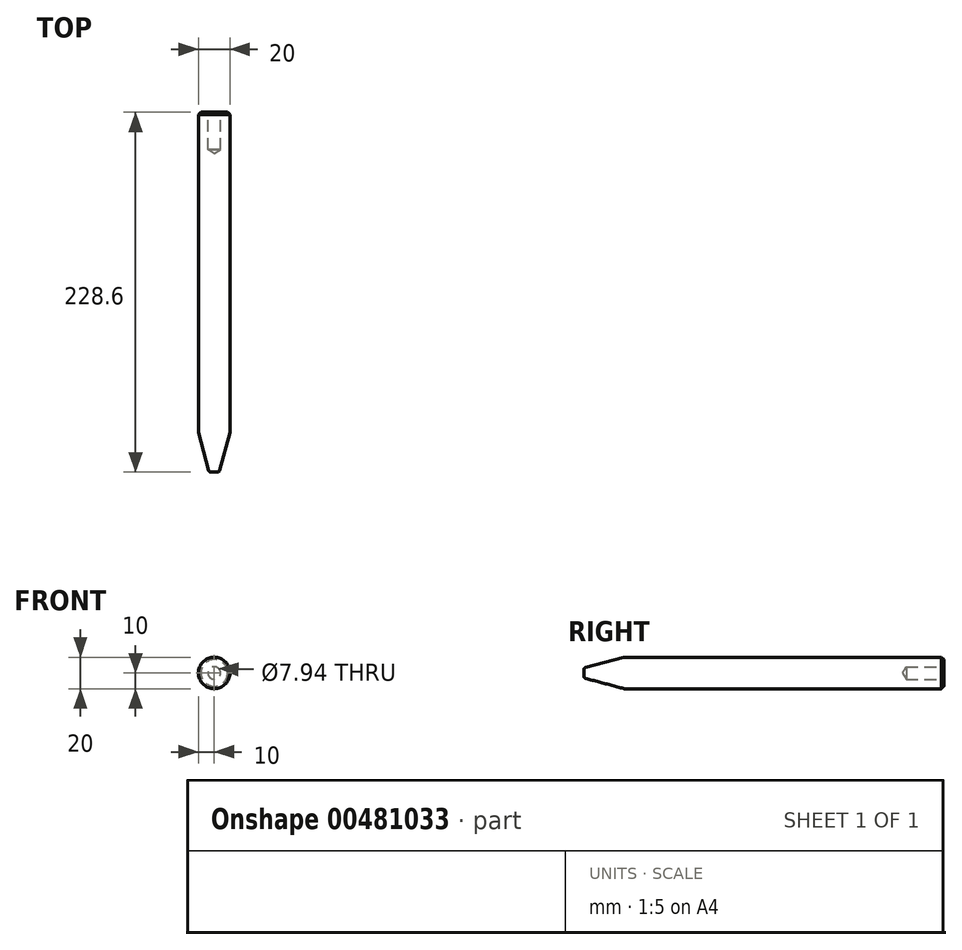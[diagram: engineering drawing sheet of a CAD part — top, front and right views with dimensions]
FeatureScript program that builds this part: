
annotation { "Feature Type Name" : "Feature", "Feature Type Description" : "" }
export const myFeature = defineFeature(function(context is Context, id is Id, definition is map)
    precondition{}
    {
        {
            var Q0;
            Q0=qCreatedBy(makeId("Right.planeOp"),FACE);
            var sketch = newSketch(context, id + "F0", { "sketchPlane" : qUnion([Q0])});
            skLineSegment(sketch, "E0", {"start": v(0, 0) * mm, "end": v(-228.6, 0) * mm});
            skLineSegment(sketch, "E1", {"start": v(-228.6, 0) * mm, "end": v(-228.6, 3.17) * mm});
            skLineSegment(sketch, "E2", {"start": v(-228.6, 3.17) * mm, "end": v(-203.13, 10) * mm});
            skLineSegment(sketch, "E3", {"start": v(-203.13, 10) * mm, "end": v(0, 10) * mm});
            skLineSegment(sketch, "E4", {"start": v(0, 10) * mm, "end": v(0, 0) * mm});
            skSolve(sketch);
        }
        {
            var Q0;
            Q0=makeQuery(id+"F0.imprint","IMPRINT",FACE,{"disambiguationData":[TD([[makeQuery(id+"F0.imprint","IMPRINT",EDGE,{"derivedFrom":sQuery(id+"F0.wireOp",EDGE,"E0")}),-1.0]])]});
            var Q1;
            Q1=sQuery(id+"F0.wireOp",EDGE,"E0");
            revolve(context, id + "F1", {"entities" : qUnion([Q0]), "axis" : qUnion([Q1]), "revolveType" : RevolveType.FULL});
        }
        {
            var Q0;
            Q0=makeQuery(id+"F1.opRevolve","SWEPT_EDGE",EDGE,{"disambiguationData":[OSD([sQuery(id+"F0.wireOp",EDGE,"E2"),sQuery(id+"F0.wireOp",EDGE,"E3")])]});
            var Q1;
            Q1=makeQuery(id+"F1.opRevolve","SWEPT_EDGE",EDGE,{"disambiguationData":[OSD([sQuery(id+"F0.wireOp",EDGE,"E1"),sQuery(id+"F0.wireOp",EDGE,"E2")])]});
            fillet(context, id + "F2", {"entities" : qUnion([Q0, Q1]), "radius" : 1.52 * mm, "tangentPropagation" : true, "allowEdgeOverflow" : false});
        }
        {
            var Q0;
            Q0=makeQuery(id+"F1.opRevolve","SWEPT_FACE",FACE,{"disambiguationData":[OSD([sQuery(id+"F0.wireOp",EDGE,"E4")])]});
            var sketch = newSketch(context, id + "F3", { "sketchPlane" : qUnion([Q0])});
            skPoint(sketch, "E5", {"position": v(0, 0) * mm});
            skSolve(sketch);
        }
        {
            var Q0;
            Q0=sQuery(id+"F3.wireOp",VERTEX,"E5");
            var Q1;
            Q1=makeQuery(id+"F1.opRevolve","SWEPT_BODY",BODY,{"disambiguationData":[OSD([sQuery(id+"F0.wireOp",EDGE,"E0"),sQuery(id+"F0.wireOp",EDGE,"E1"),sQuery(id+"F0.wireOp",EDGE,"E2"),sQuery(id+"F0.wireOp",EDGE,"E3"),sQuery(id+"F0.wireOp",EDGE,"E4")])]});
            hole(context, id + "F4", {"style" : HoleStyle.SIMPLE, "endStyle" : HoleEndStyle.BLIND, "standardTappedOrClearance" : lookupTablePath({ "standard" : "ANSI", "engagement" : "75%", "pitch" : "16 tpi", "size" : "3/8", "type" : "Tapped" }), "standardBlindInLast" : lookupTablePath({ "standard" : "ANSI", "engagement" : "75%", "pitch" : "16 tpi", "size" : "3/8", "type" : "Tapped" }), "holeDiameter" : 7.94 * mm, "showTappedDepth" : true, "holeDepth" : 23.8 * mm, "tappedDepth" : 19.05 * mm, "tapClearance" : 3, "startFromSketch" : true, "locations" : qUnion([Q0]), "scope" : qUnion([Q1]), "majorDiameter" : 9.53 * mm});
        }
        {
            var Q0;
            Q0=makeQuery(id+"F1.opRevolve","SWEPT_EDGE",EDGE,{"disambiguationData":[OSD([sQuery(id+"F0.wireOp",EDGE,"E3"),sQuery(id+"F0.wireOp",EDGE,"E4")])]});
            chamfer(context, id + "F5", {"entities" : qUnion([Q0]), "width" : 1.52 * mm, "tangentPropagation" : true});
        }
    });
